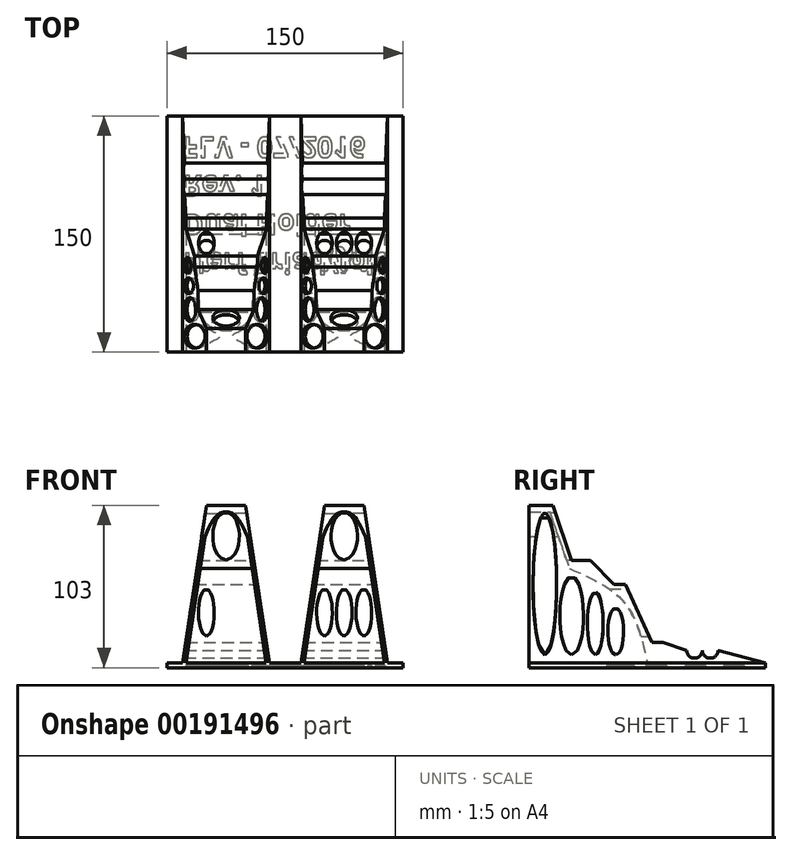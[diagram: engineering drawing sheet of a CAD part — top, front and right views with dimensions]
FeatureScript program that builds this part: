
annotation { "Feature Type Name" : "Feature", "Feature Type Description" : "" }
export const myFeature = defineFeature(function(context is Context, id is Id, definition is map)
    precondition{}
    {
        {
            var Q0;
            Q0=qCreatedBy(makeId("Top.planeOp"),FACE);
            var sketch = newSketch(context, id + "F0", { "sketchPlane" : qUnion([Q0])});
            skLineSegment(sketch, "E0.bottom", {"start": v(-75, 75) * mm, "end": v(75, 75) * mm});
            skLineSegment(sketch, "E0.top", {"start": v(-75, -75) * mm, "end": v(75, -75) * mm});
            skLineSegment(sketch, "E0.left", {"start": v(-75, 75) * mm, "end": v(-75, -75) * mm});
            skLineSegment(sketch, "E0.right", {"start": v(75, 75) * mm, "end": v(75, -75) * mm});
            skSolve(sketch);
        }
        {
            var Q0;
            Q0 = qSketchRegion(id + "F0", true);
            extrude(context, id + "F1", {"entities" : qUnion([Q0]), "depth" : 3 * mm});
        }
        {
            var Q0;
            Q0=makeQuery(id+"F1.opExtrude","SWEPT_FACE",FACE,{"disambiguationData":[OSD([sQuery(id+"F0.wireOp",EDGE,"E0.top")])]});
            var sketch = newSketch(context, id + "F2", { "sketchPlane" : qUnion([Q0])});
            skLineSegment(sketch, "E1.bottom", {"start": v(-75, 3) * mm, "end": v(75, 3) * mm});
            skLineSegment(sketch, "E1.top", {"start": v(-75, 103) * mm, "end": v(75, 103) * mm});
            skLineSegment(sketch, "E1.left", {"start": v(-75, 3) * mm, "end": v(-75, 103) * mm});
            skLineSegment(sketch, "E1.right", {"start": v(75, 3) * mm, "end": v(75, 103) * mm});
            skLineSegment(sketch, "E2", {"start": v(0, 3) * mm, "end": v(0, 103) * mm});
            skLineSegment(sketch, "E3", {"start": v(-50, 103) * mm, "end": v(-65, 3) * mm});
            skLineSegment(sketch, "E4", {"start": v(-25, 103) * mm, "end": v(-10, 3) * mm});
            skLineSegment(sketch, "E5", {"start": v(25, 103) * mm, "end": v(10, 3) * mm});
            skLineSegment(sketch, "E6", {"start": v(50, 103) * mm, "end": v(65, 3) * mm});
            skLineSegment(sketch, "E7", {"start": v(-62.98, 3) * mm, "end": v(-50.98, 83) * mm});
            skLineSegment(sketch, "E8", {"start": v(-12.02, 3) * mm, "end": v(-24.02, 83) * mm});
            skLineSegment(sketch, "E9", {"start": v(12.02, 3) * mm, "end": v(24.02, 83) * mm});
            skLineSegment(sketch, "E10", {"start": v(62.98, 3) * mm, "end": v(50.98, 83) * mm});
            skFitSpline(sketch, "E11", {"points": [v(-50.98, 83) * mm, v(-37.5, 99) * mm, v(-24.02, 83) * mm], "startDerivative": vector(32.87, 84) * mm, "endDerivative": vector(32.87, -84) * mm});
            skFitSpline(sketch, "E12", {"points": [v(24.02, 83) * mm, v(37.5, 99) * mm, v(50.98, 83) * mm], "startDerivative": vector(32.87, 84) * mm, "endDerivative": vector(32.87, -84) * mm});
            skSolve(sketch);
        }
        {
            var Q0;
            Q0=makeQuery(id+"F1.opExtrude","SWEPT_FACE",FACE,{"disambiguationData":[OSD([sQuery(id+"F0.wireOp",EDGE,"E0.right")])]});
            var sketch = newSketch(context, id + "F3", { "sketchPlane" : qUnion([Q0])});
            skLineSegment(sketch, "E13.bottom", {"start": v(-75, 3) * mm, "end": v(75, 3) * mm});
            skLineSegment(sketch, "E13.top", {"start": v(-75, 103) * mm, "end": v(75, 103) * mm});
            skLineSegment(sketch, "E13.left", {"start": v(-75, 3) * mm, "end": v(-75, 103) * mm});
            skLineSegment(sketch, "E13.right", {"start": v(75, 3) * mm, "end": v(75, 103) * mm});
            skLineSegment(sketch, "E14", {"start": v(-60, 103) * mm, "end": v(-48, 68) * mm});
            skLineSegment(sketch, "E15", {"start": v(-48, 68) * mm, "end": v(-36, 68) * mm});
            skLineSegment(sketch, "E16", {"start": v(-36, 68) * mm, "end": v(-21, 53) * mm});
            skLineSegment(sketch, "E17", {"start": v(-21, 53) * mm, "end": v(-14, 53) * mm});
            skLineSegment(sketch, "E18", {"start": v(-14, 53) * mm, "end": v(3, 16) * mm});
            skLineSegment(sketch, "E19", {"start": v(3, 16) * mm, "end": v(10, 16) * mm});
            skLineSegment(sketch, "E20", {"start": v(10, 16) * mm, "end": v(25, 11) * mm});
            skLineSegment(sketch, "E21", {"start": v(25, 11) * mm, "end": v(45, 11) * mm});
            skLineSegment(sketch, "E22", {"start": v(45, 11) * mm, "end": v(75, 3) * mm});
            skLineSegment(sketch, "E23", {"start": v(-63.17, 103) * mm, "end": v(-49.46, 63) * mm});
            skFitSpline(sketch, "E24", {"points": [v(-49.46, 63) * mm, v(-14.36, 41.18) * mm, v(0, 3) * mm], "startDerivative": vector(80.28, -35.19) * mm, "endDerivative": vector(18.56, -84.87) * mm});
            skSolve(sketch);
        }
        {
            var Q0;
            {var subQ0=sQuery(id+"F2.wireOp",EDGE,"E3");Q0=makeQuery(id+"F2.imprint","IMPRINT",FACE,{"disambiguationData":[TD([[makeQuery(id+"F2.imprint","IMPRINT",EDGE,{"derivedFrom":subQ0}),1.0]])]});}
            var Q1;
            {var subQ0=sQuery(id+"F2.wireOp",EDGE,"E5");Q1=makeQuery(id+"F2.imprint","IMPRINT",FACE,{"disambiguationData":[TD([[makeQuery(id+"F2.imprint","IMPRINT",EDGE,{"derivedFrom":subQ0}),1.0]])]});}
            var Q2;
            Q2=makeQuery(id+"F1.opExtrude","SWEPT_FACE",FACE,{"disambiguationData":[OSD([sQuery(id+"F0.wireOp",EDGE,"E0.bottom")])]});
            extrude(context, id + "F4", {"entities" : qUnion([Q0, Q1]), "operationType" : NewBodyOperationType.ADD, "endBound" : BoundingType.UP_TO_SURFACE, "oppositeDirection" : true, "endBoundEntityFace" : qUnion([Q2]), "depth" : 25 * mm});
        }
        {
            var Q0;
            {var subQ0=sQuery(id+"F3.wireOp",EDGE,"E14");Q0=makeQuery(id+"F3.imprint","IMPRINT",FACE,{"disambiguationData":[TD([[makeQuery(id+"F3.imprint","IMPRINT",EDGE,{"derivedFrom":subQ0}),-1.0]])]});}
            var Q1;
            Q1=makeQuery(id+"F1.opExtrude","SWEPT_FACE",FACE,{"disambiguationData":[OSD([sQuery(id+"F0.wireOp",EDGE,"E0.left")])]});
            extrude(context, id + "F5", {"entities" : qUnion([Q0]), "operationType" : NewBodyOperationType.ADD, "endBound" : BoundingType.UP_TO_SURFACE, "oppositeDirection" : true, "endBoundEntityFace" : qUnion([Q1]), "depth" : 25 * mm});
        }
        {
            var Q0;
            {var subQ0=sQuery(id+"F2.wireOp",EDGE,"E1.left");Q0=makeQuery(id+"F2.imprint","IMPRINT",FACE,{"disambiguationData":[TD([[makeQuery(id+"F2.imprint","IMPRINT",EDGE,{"derivedFrom":subQ0}),-1.0]])]});}
            var Q1;
            {var subQ0=sQuery(id+"F2.wireOp",EDGE,"E2");Q1=makeQuery(id+"F2.imprint","IMPRINT",FACE,{"disambiguationData":[TD([[makeQuery(id+"F2.imprint","IMPRINT",EDGE,{"derivedFrom":subQ0}),1.0]])]});}
            var Q2;
            {var subQ0=sQuery(id+"F2.wireOp",EDGE,"E2");Q2=makeQuery(id+"F2.imprint","IMPRINT",FACE,{"disambiguationData":[TD([[makeQuery(id+"F2.imprint","IMPRINT",EDGE,{"derivedFrom":subQ0}),-1.0]])]});}
            var Q3;
            {var subQ0=sQuery(id+"F2.wireOp",EDGE,"E1.right");Q3=makeQuery(id+"F2.imprint","IMPRINT",FACE,{"disambiguationData":[TD([[makeQuery(id+"F2.imprint","IMPRINT",EDGE,{"derivedFrom":subQ0}),1.0]])]});}
            var Q4;
            {var subQ0=sQuery(id+"F2.wireOp",EDGE,"E1.top");var subQ1=sQuery(id+"F2.wireOp",EDGE,"E1.bottom");var subQ2=sQuery(id+"F0.wireOp",EDGE,"E0.bottom");Q4=makeQuery(id+"F4.boolean.opBoolean","MERGE",FACE,{"derivedFrom":[makeQuery(id+"F1.opExtrude","SWEPT_FACE",FACE,{"disambiguationData":[OSD([subQ2])]}),makeQuery(id+"F4.opExtrude","CAP_FACE",FACE,{"disambiguationData":[OSD([subQ2]),ownerDisambiguation([makeQuery(id+"F4.opExtrude","SWEPT_BODY",BODY,{"disambiguationData":[OSD([subQ1,subQ0,sQuery(id+"F2.wireOp",EDGE,"E3"),sQuery(id+"F2.wireOp",EDGE,"E4"),sQuery(id+"F2.wireOp",EDGE,"E7"),sQuery(id+"F2.wireOp",EDGE,"E8"),sQuery(id+"F2.wireOp",EDGE,"ciHklE4U-pB17-gafY-pSRJ-bKM6XeZEa9pb")])]})])],"isStart":false}),makeQuery(id+"F4.opExtrude","CAP_FACE",FACE,{"disambiguationData":[OSD([subQ2]),ownerDisambiguation([makeQuery(id+"F4.opExtrude","SWEPT_BODY",BODY,{"disambiguationData":[OSD([subQ1,subQ0,sQuery(id+"F2.wireOp",EDGE,"E5"),sQuery(id+"F2.wireOp",EDGE,"E6"),sQuery(id+"F2.wireOp",EDGE,"E9"),sQuery(id+"F2.wireOp",EDGE,"E10"),sQuery(id+"F2.wireOp",EDGE,"xGXNXY8u-arDx-ufjF-TU0i-VHOFZnnzQfJi")])]})])],"isStart":false})]});}
            extrude(context, id + "F6", {"entities" : qUnion([Q0, Q1, Q2, Q3]), "operationType" : NewBodyOperationType.REMOVE, "endBound" : BoundingType.UP_TO_SURFACE, "oppositeDirection" : true, "endBoundEntityFace" : qUnion([Q4]), "depth" : 25 * mm});
        }
        {
            var Q0;
            {var subQ1=sQuery(id+"F3.wireOp",EDGE,"E13.right");Q0=makeQuery(id+"F3.imprint","IMPRINT",FACE,{"disambiguationData":[TD([[makeQuery(id+"F3.imprint","IMPRINT",EDGE,{"derivedFrom":subQ1}),1.0]])]});}
            var Q1;
            {var subQ0=sQuery(id+"F0.wireOp",EDGE,"E0.left");Q1=makeQuery(id+"F5.boolean.opBoolean","MERGE",FACE,{"derivedFrom":[makeQuery(id+"F1.opExtrude","SWEPT_FACE",FACE,{"disambiguationData":[OSD([subQ0])]}),makeQuery(id+"F5.opExtrude","CAP_FACE",FACE,{"disambiguationData":[OSD([subQ0])],"isStart":false})]});}
            extrude(context, id + "F7", {"entities" : qUnion([Q0]), "operationType" : NewBodyOperationType.REMOVE, "endBound" : BoundingType.UP_TO_SURFACE, "oppositeDirection" : true, "endBoundEntityFace" : qUnion([Q1]), "depth" : 25 * mm});
        }
        {
            var Q0;
            {var subQ0=sQuery(id+"F0.wireOp",EDGE,"E0.right");Q0=makeQuery(id+"F3.imprint","IMPRINT",FACE,{"disambiguationData":[TD([[makeQuery(id+"F3.imprint","IMPRINT",EDGE,{"derivedFrom":makeQuery(id+"F1.opExtrude","CAP_EDGE",EDGE,{"disambiguationData":[OSD([subQ0])],"isStart":true})}),-1.0]])]});}
            var sketch = newSketch(context, id + "F8", { "sketchPlane" : qUnion([Q0])});
            skEllipse(sketch, "E25", {"center": v(-65, 53) * mm, "majorRadius": 45 * mm, "minorRadius": 7.5 * mm, "majorAxis": v(0, -1)});
            skEllipse(sketch, "E26", {"center": v(-48, 33) * mm, "majorRadius": 25 * mm, "minorRadius": 7.5 * mm, "majorAxis": v(0, -1)});
            skEllipse(sketch, "E27", {"center": v(-33, 28) * mm, "majorRadius": 20 * mm, "minorRadius": 5 * mm, "majorAxis": v(0, -1)});
            skEllipse(sketch, "E28", {"center": v(-20, 23) * mm, "majorRadius": 15 * mm, "minorRadius": 5 * mm, "majorAxis": v(0, -1)});
            skSolve(sketch);
        }
        {
            var Q0;
            Q0=makeQuery(id+"F8.imprint","IMPRINT",FACE,{"disambiguationData":[TD([[makeQuery(id+"F8.imprint","IMPRINT",EDGE,{"derivedFrom":sQuery(id+"F8.wireOp",EDGE,"E26")}),1.0]])]});
            var Q1;
            Q1=makeQuery(id+"F8.imprint","IMPRINT",FACE,{"disambiguationData":[TD([[makeQuery(id+"F8.imprint","IMPRINT",EDGE,{"derivedFrom":sQuery(id+"F8.wireOp",EDGE,"E25")}),1.0]])]});
            var Q2;
            Q2=makeQuery(id+"F8.imprint","IMPRINT",FACE,{"disambiguationData":[TD([[makeQuery(id+"F8.imprint","IMPRINT",EDGE,{"derivedFrom":sQuery(id+"F8.wireOp",EDGE,"E27")}),1.0]])]});
            var Q3;
            Q3=makeQuery(id+"F8.imprint","IMPRINT",FACE,{"disambiguationData":[TD([[makeQuery(id+"F8.imprint","IMPRINT",EDGE,{"derivedFrom":sQuery(id+"F8.wireOp",EDGE,"E28")}),1.0]])]});
            var Q4;
            {var subQ0=sQuery(id+"F0.wireOp",EDGE,"E0.left");Q4=makeQuery(id+"F5.boolean.opBoolean","MERGE",FACE,{"derivedFrom":[makeQuery(id+"F1.opExtrude","SWEPT_FACE",FACE,{"disambiguationData":[OSD([subQ0])]}),makeQuery(id+"F5.opExtrude","CAP_FACE",FACE,{"disambiguationData":[OSD([subQ0])],"isStart":false})]});}
            extrude(context, id + "F9", {"entities" : qUnion([Q0, Q1, Q2, Q3]), "operationType" : NewBodyOperationType.REMOVE, "endBound" : BoundingType.UP_TO_SURFACE, "oppositeDirection" : true, "endBoundEntityFace" : qUnion([Q4]), "depth" : 25 * mm});
        }
        {
            var Q0;
            {var subQ0=sQuery(id+"F2.wireOp",EDGE,"E1.top");var subQ1=sQuery(id+"F2.wireOp",EDGE,"E1.bottom");var subQ2=sQuery(id+"F0.wireOp",EDGE,"E0.bottom");Q0=makeQuery(id+"F4.boolean.opBoolean","MERGE",FACE,{"derivedFrom":[makeQuery(id+"F1.opExtrude","SWEPT_FACE",FACE,{"disambiguationData":[OSD([subQ2])]}),makeQuery(id+"F4.opExtrude","CAP_FACE",FACE,{"disambiguationData":[OSD([subQ2]),ownerDisambiguation([makeQuery(id+"F4.opExtrude","SWEPT_BODY",BODY,{"disambiguationData":[OSD([subQ1,subQ0,sQuery(id+"F2.wireOp",EDGE,"E3"),sQuery(id+"F2.wireOp",EDGE,"E4"),sQuery(id+"F2.wireOp",EDGE,"E7"),sQuery(id+"F2.wireOp",EDGE,"E8"),sQuery(id+"F2.wireOp",EDGE,"E11")])]})])],"isStart":false}),makeQuery(id+"F4.opExtrude","CAP_FACE",FACE,{"disambiguationData":[OSD([subQ2]),ownerDisambiguation([makeQuery(id+"F4.opExtrude","SWEPT_BODY",BODY,{"disambiguationData":[OSD([subQ1,subQ0,sQuery(id+"F2.wireOp",EDGE,"E5"),sQuery(id+"F2.wireOp",EDGE,"E6"),sQuery(id+"F2.wireOp",EDGE,"E9"),sQuery(id+"F2.wireOp",EDGE,"E10"),sQuery(id+"F2.wireOp",EDGE,"E12")])]})])],"isStart":false})]});}
            var sketch = newSketch(context, id + "F10", { "sketchPlane" : qUnion([Q0])});
            skLineSegment(sketch, "E29.bottom", {"start": v(-75, 3) * mm, "end": v(75, 3) * mm});
            skLineSegment(sketch, "E29.top", {"start": v(-75, 103) * mm, "end": v(75, 103) * mm});
            skLineSegment(sketch, "E29.left", {"start": v(-75, 3) * mm, "end": v(-75, 103) * mm});
            skLineSegment(sketch, "E29.right", {"start": v(75, 3) * mm, "end": v(75, 103) * mm});
            skLineSegment(sketch, "E30", {"start": v(0, 103) * mm, "end": v(0, 3) * mm});
            skEllipse(sketch, "E31", {"center": v(-50, 35) * mm, "majorRadius": 15 * mm, "minorRadius": 5 * mm, "majorAxis": v(0, -1)});
            skEllipse(sketch, "E32", {"center": v(-37.5, 35) * mm, "majorRadius": 15 * mm, "minorRadius": 5 * mm, "majorAxis": v(0, -1)});
            skEllipse(sketch, "E33", {"center": v(-25, 35) * mm, "majorRadius": 15 * mm, "minorRadius": 5 * mm, "majorAxis": v(0, -1)});
            skEllipse(sketch, "E34.MirrorC", {"center": v(50, 35) * mm, "majorRadius": 15 * mm, "minorRadius": 5 * mm, "majorAxis": v(0, -1)});
            skEllipse(sketch, "E35.MirrorC", {"center": v(25, 35) * mm, "majorRadius": 15 * mm, "minorRadius": 5 * mm, "majorAxis": v(0, -1)});
            skEllipse(sketch, "E36.MirrorC", {"center": v(37.5, 35) * mm, "majorRadius": 15 * mm, "minorRadius": 5 * mm, "majorAxis": v(0, -1)});
            skEllipse(sketch, "E37.MirrorC", {"center": v(25, 35) * mm, "majorRadius": 15 * mm, "minorRadius": 5 * mm, "majorAxis": v(0, -1)});
            skEllipse(sketch, "E38.MirrorC", {"center": v(37.5, 35) * mm, "majorRadius": 15 * mm, "minorRadius": 5 * mm, "majorAxis": v(0, -1)});
            skEllipse(sketch, "E39", {"center": v(-37.5, 83.56) * mm, "majorRadius": 15 * mm, "minorRadius": 8.45 * mm, "majorAxis": v(0, -1)});
            skEllipse(sketch, "E40.MirrorC", {"center": v(37.5, 83.56) * mm, "majorRadius": 15 * mm, "minorRadius": 8.45 * mm, "majorAxis": v(0, -1)});
            skSolve(sketch);
        }
        {
            var Q0;
            Q0=makeQuery(id+"F10.imprint","IMPRINT",FACE,{"disambiguationData":[TD([[makeQuery(id+"F10.imprint","IMPRINT",EDGE,{"derivedFrom":sQuery(id+"F10.wireOp",EDGE,"E31")}),1.0]])]});
            var Q1;
            Q1=makeQuery(id+"F10.imprint","IMPRINT",FACE,{"disambiguationData":[TD([[makeQuery(id+"F10.imprint","IMPRINT",EDGE,{"derivedFrom":sQuery(id+"F10.wireOp",EDGE,"E32")}),1.0]])]});
            var Q2;
            Q2=makeQuery(id+"F10.imprint","IMPRINT",FACE,{"disambiguationData":[TD([[makeQuery(id+"F10.imprint","IMPRINT",EDGE,{"derivedFrom":sQuery(id+"F10.wireOp",EDGE,"E33")}),1.0]])]});
            var Q3;
            Q3=makeQuery(id+"F10.imprint","IMPRINT",FACE,{"disambiguationData":[TD([[makeQuery(id+"F10.imprint","IMPRINT",EDGE,{"derivedFrom":sQuery(id+"F10.wireOp",EDGE,"E37.MirrorC")}),1.0]])]});
            var Q4;
            Q4=makeQuery(id+"F10.imprint","IMPRINT",FACE,{"disambiguationData":[TD([[makeQuery(id+"F10.imprint","IMPRINT",EDGE,{"derivedFrom":sQuery(id+"F10.wireOp",EDGE,"E34.MirrorC")}),1.0]])]});
            var Q5;
            Q5=makeQuery(id+"F10.imprint","IMPRINT",FACE,{"disambiguationData":[TD([[makeQuery(id+"F10.imprint","IMPRINT",EDGE,{"derivedFrom":sQuery(id+"F10.wireOp",EDGE,"E38.MirrorC")}),1.0]])]});
            var Q6;
            Q6=makeQuery(id+"F10.imprint","IMPRINT",FACE,{"disambiguationData":[TD([[makeQuery(id+"F10.imprint","IMPRINT",EDGE,{"derivedFrom":sQuery(id+"F10.wireOp",EDGE,"E39")}),1.0]])]});
            var Q7;
            Q7=makeQuery(id+"F10.imprint","IMPRINT",FACE,{"disambiguationData":[TD([[makeQuery(id+"F10.imprint","IMPRINT",EDGE,{"derivedFrom":sQuery(id+"F10.wireOp",EDGE,"E40.MirrorC")}),1.0]])]});
            var Q8;
            {var subQ0=sQuery(id+"F2.wireOp",EDGE,"E1.top");var subQ1=sQuery(id+"F2.wireOp",EDGE,"E1.bottom");Q8=makeQuery(id+"F4.boolean.opBoolean","MERGE",FACE,{"derivedFrom":[makeQuery(id+"F1.opExtrude","SWEPT_FACE",FACE,{"disambiguationData":[OSD([sQuery(id+"F0.wireOp",EDGE,"E0.top")])]}),makeQuery(id+"F4.opExtrude","CAP_FACE",FACE,{"disambiguationData":[OSD([subQ1,subQ0,sQuery(id+"F2.wireOp",EDGE,"E3"),sQuery(id+"F2.wireOp",EDGE,"E4"),sQuery(id+"F2.wireOp",EDGE,"E7"),sQuery(id+"F2.wireOp",EDGE,"E8"),sQuery(id+"F2.wireOp",EDGE,"E11")])],"isStart":true}),makeQuery(id+"F4.opExtrude","CAP_FACE",FACE,{"disambiguationData":[OSD([subQ1,subQ0,sQuery(id+"F2.wireOp",EDGE,"E5"),sQuery(id+"F2.wireOp",EDGE,"E6"),sQuery(id+"F2.wireOp",EDGE,"E9"),sQuery(id+"F2.wireOp",EDGE,"E10"),sQuery(id+"F2.wireOp",EDGE,"E12")])],"isStart":true})]});}
            extrude(context, id + "F11", {"entities" : qUnion([Q0, Q1, Q2, Q3, Q4, Q5, Q6, Q7]), "operationType" : NewBodyOperationType.REMOVE, "endBound" : BoundingType.UP_TO_SURFACE, "oppositeDirection" : true, "endBoundEntityFace" : qUnion([Q8]), "depth" : 25 * mm});
        }
        {
            var Q0;
            {var subQ0=sQuery(id+"F0.wireOp",EDGE,"E0.right");Q0=makeQuery(id+"F3.imprint","IMPRINT",FACE,{"disambiguationData":[TD([[makeQuery(id+"F3.imprint","IMPRINT",EDGE,{"derivedFrom":makeQuery(id+"F1.opExtrude","CAP_EDGE",EDGE,{"disambiguationData":[OSD([subQ0])],"isStart":true})}),-1.0]])]});}
            cPlane(context, id + "F12", {"entities" : qUnion([Q0]), "cplaneType" : CPlaneType.OFFSET, "offset" : 37.5 * mm, "oppositeDirection" : true, "width" : 150 * mm, "height" : 150 * mm});
        }
        {
            var Q0;
            {var subQ0=sQuery(id+"F3.wireOp",EDGE,"E21");Q0=makeQuery(id+"F7.boolean.opBoolean","MERGE",FACE,{"derivedFrom":[makeQuery(id+"F5.boolean.opBoolean","SPLIT",FACE,{"disambiguationData":[TD([makeQuery(id+"F4.opExtrude","SWEPT_FACE",FACE,{"disambiguationData":[OSD([sQuery(id+"F2.wireOp",EDGE,"E7")])]})])],"derivedFrom":makeQuery(id+"F5.opExtrude","SWEPT_FACE",FACE,{"disambiguationData":[OSD([subQ0])]})}),makeQuery(id+"F7.opExtrude","SWEPT_FACE",FACE,{"disambiguationData":[OSD([subQ0])]})]});}
            var sketch = newSketch(context, id + "F13", { "sketchPlane" : qUnion([Q0])});
            skLineSegment(sketch, "E41.bottom", {"start": v(-64.8, 45) * mm, "end": v(-10.2, 45) * mm});
            skLineSegment(sketch, "E41.top", {"start": v(-64.8, 25) * mm, "end": v(-10.2, 25) * mm});
            skLineSegment(sketch, "E41.left", {"start": v(-64.8, 45) * mm, "end": v(-64.8, 25) * mm});
            skLineSegment(sketch, "E41.right", {"start": v(-10.2, 45) * mm, "end": v(-10.2, 25) * mm});
            skLineSegment(sketch, "E42", {"start": v(-64.8, 35) * mm, "end": v(-10.2, 35) * mm});
            skLineSegment(sketch, "E43", {"start": v(-64.8, 30) * mm, "end": v(-10.2, 30) * mm});
            skLineSegment(sketch, "E44", {"start": v(-10.2, 40) * mm, "end": v(-64.8, 40) * mm});
            skSolve(sketch);
        }
        {
            var Q0;
            {var subQ0=sQuery(id+"F13.wireOp",EDGE,"E42");var subQ1=sQuery(id+"F3.wireOp",EDGE,"E21");var subQ2=makeQuery(id+"F7.opExtrude","SWEPT_FACE",FACE,{"disambiguationData":[OSD([subQ1])]});var subQ3=sQuery(id+"F2.wireOp",EDGE,"E3");var subQ5=sQuery(id+"F0.wireOp",EDGE,"E0.bottom");var subQ6=makeQuery(id+"F1.opExtrude","SWEPT_FACE",FACE,{"disambiguationData":[OSD([subQ5])]});var subQ31=makeQuery(id+"F4.opExtrude","SWEPT_FACE",FACE,{"disambiguationData":[OSD([subQ3])]});var subQ34=sQuery(id+"F0.wireOp",EDGE,"E0.top");var subQ35=makeQuery(id+"F1.opExtrude","SWEPT_FACE",FACE,{"disambiguationData":[OSD([subQ34])]});var subQ39=makeQuery(id+"F7.boolean.opBoolean","INTERSECT",EDGE,{"derivedFrom":[makeQuery(id+"F6.boolean.opBoolean","MERGE",FACE,{"derivedFrom":[makeQuery(id+"F5.boolean.opBoolean","SPLIT",FACE,{"disambiguationData":[TD([subQ35])],"derivedFrom":subQ31}),makeQuery(id+"F5.boolean.opBoolean","SPLIT",FACE,{"disambiguationData":[TD([subQ6])],"derivedFrom":subQ31}),makeQuery(id+"F6.opExtrude","SWEPT_FACE",FACE,{"disambiguationData":[OSD([subQ3])]})]}),subQ2]});var subQ40=makeQuery(id+"F13.imprint","INTERSECT",VERTEX,{"derivedFrom":[subQ39,subQ0]});Q0=makeQuery(id+"F13.imprint","IMPRINT",FACE,{"disambiguationData":[TD([[makeQuery(id+"F13.imprint","IMPRINT",EDGE,{"disambiguationData":[TD([[subQ40,-1.0]])],"derivedFrom":subQ0}),1.0]])]});}
            var Q1;
            {var subQ0=sQuery(id+"F13.wireOp",EDGE,"E42");var subQ1=sQuery(id+"F13.wireOp",EDGE,"E41.right");var subQ2=makeQuery(id+"F13.imprint","INTERSECT",VERTEX,{"derivedFrom":[subQ1,subQ0]});Q1=makeQuery(id+"F13.imprint","IMPRINT",FACE,{"disambiguationData":[TD([[makeQuery(id+"F13.imprint","IMPRINT",EDGE,{"disambiguationData":[TD([[subQ2,1.0]])],"derivedFrom":subQ1}),-1.0]])]});}
            var Q2;
            {var subQ0=sQuery(id+"F13.wireOp",EDGE,"E42");var subQ1=sQuery(id+"F13.wireOp",EDGE,"E41.left");var subQ2=makeQuery(id+"F13.imprint","INTERSECT",VERTEX,{"derivedFrom":[subQ1,subQ0]});Q2=makeQuery(id+"F13.imprint","IMPRINT",FACE,{"disambiguationData":[TD([[makeQuery(id+"F13.imprint","IMPRINT",EDGE,{"disambiguationData":[TD([[subQ2,1.0]])],"derivedFrom":subQ1}),1.0]])]});}
            var Q3;
            Q3=sQuery(id+"F13.wireOp",EDGE,"E44");
            revolve(context, id + "F14", {"operationType" : NewBodyOperationType.REMOVE, "entities" : qUnion([Q0, Q1, Q2]), "axis" : qUnion([Q3]), "revolveType" : RevolveType.FULL, "oppositeDirection" : true});
        }
        {
            var Q0;
            {var subQ0=sQuery(id+"F13.wireOp",EDGE,"E42");var subQ1=sQuery(id+"F3.wireOp",EDGE,"E21");var subQ2=makeQuery(id+"F7.opExtrude","SWEPT_FACE",FACE,{"disambiguationData":[OSD([subQ1])]});var subQ3=sQuery(id+"F2.wireOp",EDGE,"E3");var subQ5=sQuery(id+"F0.wireOp",EDGE,"E0.bottom");var subQ6=makeQuery(id+"F1.opExtrude","SWEPT_FACE",FACE,{"disambiguationData":[OSD([subQ5])]});var subQ31=makeQuery(id+"F4.opExtrude","SWEPT_FACE",FACE,{"disambiguationData":[OSD([subQ3])]});var subQ34=sQuery(id+"F0.wireOp",EDGE,"E0.top");var subQ35=makeQuery(id+"F1.opExtrude","SWEPT_FACE",FACE,{"disambiguationData":[OSD([subQ34])]});var subQ39=makeQuery(id+"F7.boolean.opBoolean","INTERSECT",EDGE,{"derivedFrom":[makeQuery(id+"F6.boolean.opBoolean","MERGE",FACE,{"derivedFrom":[makeQuery(id+"F5.boolean.opBoolean","SPLIT",FACE,{"disambiguationData":[TD([subQ35])],"derivedFrom":subQ31}),makeQuery(id+"F5.boolean.opBoolean","SPLIT",FACE,{"disambiguationData":[TD([subQ6])],"derivedFrom":subQ31}),makeQuery(id+"F6.opExtrude","SWEPT_FACE",FACE,{"disambiguationData":[OSD([subQ3])]})]}),subQ2]});var subQ40=makeQuery(id+"F13.imprint","INTERSECT",VERTEX,{"derivedFrom":[subQ39,subQ0]});Q0=makeQuery(id+"F13.imprint","IMPRINT",FACE,{"disambiguationData":[TD([[makeQuery(id+"F13.imprint","IMPRINT",EDGE,{"disambiguationData":[TD([[subQ40,-1.0]])],"derivedFrom":subQ0}),-1.0]])]});}
            var Q1;
            {var subQ0=sQuery(id+"F13.wireOp",EDGE,"E42");var subQ1=sQuery(id+"F13.wireOp",EDGE,"E41.left");var subQ2=makeQuery(id+"F13.imprint","INTERSECT",VERTEX,{"derivedFrom":[subQ1,subQ0]});Q1=makeQuery(id+"F13.imprint","IMPRINT",FACE,{"disambiguationData":[TD([[makeQuery(id+"F13.imprint","IMPRINT",EDGE,{"disambiguationData":[TD([[subQ2,-1.0]])],"derivedFrom":subQ1}),1.0]])]});}
            var Q2;
            {var subQ0=sQuery(id+"F13.wireOp",EDGE,"E42");var subQ1=sQuery(id+"F13.wireOp",EDGE,"E41.right");var subQ2=makeQuery(id+"F13.imprint","INTERSECT",VERTEX,{"derivedFrom":[subQ1,subQ0]});Q2=makeQuery(id+"F13.imprint","IMPRINT",FACE,{"disambiguationData":[TD([[makeQuery(id+"F13.imprint","IMPRINT",EDGE,{"disambiguationData":[TD([[subQ2,-1.0]])],"derivedFrom":subQ1}),-1.0]])]});}
            var Q3;
            Q3=sQuery(id+"F13.wireOp",EDGE,"E43");
            revolve(context, id + "F15", {"operationType" : NewBodyOperationType.REMOVE, "entities" : qUnion([Q0, Q1, Q2]), "axis" : qUnion([Q3]), "revolveType" : RevolveType.FULL, "oppositeDirection" : true});
        }
        {
            var Q0;
            {var subQ0=sQuery(id+"F3.wireOp",EDGE,"E21");Q0=makeQuery(id+"F7.boolean.opBoolean","MERGE",FACE,{"derivedFrom":[makeQuery(id+"F5.boolean.opBoolean","SPLIT",FACE,{"disambiguationData":[TD([makeQuery(id+"F4.opExtrude","SWEPT_FACE",FACE,{"disambiguationData":[OSD([sQuery(id+"F2.wireOp",EDGE,"E9")])]})])],"derivedFrom":makeQuery(id+"F5.opExtrude","SWEPT_FACE",FACE,{"disambiguationData":[OSD([subQ0])]})}),makeQuery(id+"F7.opExtrude","SWEPT_FACE",FACE,{"disambiguationData":[OSD([subQ0])]})]});}
            var sketch = newSketch(context, id + "F16", { "sketchPlane" : qUnion([Q0])});
            skLineSegment(sketch, "E45.bottom", {"start": v(10.2, 45) * mm, "end": v(64.8, 45) * mm});
            skLineSegment(sketch, "E45.top", {"start": v(10.2, 25) * mm, "end": v(64.8, 25) * mm});
            skLineSegment(sketch, "E45.left", {"start": v(10.2, 45) * mm, "end": v(10.2, 25) * mm});
            skLineSegment(sketch, "E45.right", {"start": v(64.8, 45) * mm, "end": v(64.8, 25) * mm});
            skLineSegment(sketch, "E46", {"start": v(10.2, 35) * mm, "end": v(64.8, 35) * mm});
            skLineSegment(sketch, "E47", {"start": v(64.8, 30) * mm, "end": v(10.2, 30) * mm});
            skLineSegment(sketch, "E48", {"start": v(10.2, 40) * mm, "end": v(64.8, 40) * mm});
            skSolve(sketch);
        }
        {
            var Q0;
            {var subQ0=sQuery(id+"F16.wireOp",EDGE,"E46");var subQ1=sQuery(id+"F3.wireOp",EDGE,"E21");var subQ2=makeQuery(id+"F7.opExtrude","SWEPT_FACE",FACE,{"disambiguationData":[OSD([subQ1])]});var subQ3=sQuery(id+"F2.wireOp",EDGE,"E5");var subQ5=sQuery(id+"F0.wireOp",EDGE,"E0.bottom");var subQ6=makeQuery(id+"F1.opExtrude","SWEPT_FACE",FACE,{"disambiguationData":[OSD([subQ5])]});var subQ31=makeQuery(id+"F4.opExtrude","SWEPT_FACE",FACE,{"disambiguationData":[OSD([subQ3])]});var subQ34=sQuery(id+"F0.wireOp",EDGE,"E0.top");var subQ35=makeQuery(id+"F1.opExtrude","SWEPT_FACE",FACE,{"disambiguationData":[OSD([subQ34])]});var subQ39=makeQuery(id+"F7.boolean.opBoolean","INTERSECT",EDGE,{"derivedFrom":[makeQuery(id+"F6.boolean.opBoolean","MERGE",FACE,{"derivedFrom":[makeQuery(id+"F5.boolean.opBoolean","SPLIT",FACE,{"disambiguationData":[TD([subQ35])],"derivedFrom":subQ31}),makeQuery(id+"F5.boolean.opBoolean","SPLIT",FACE,{"disambiguationData":[TD([subQ6])],"derivedFrom":subQ31}),makeQuery(id+"F6.opExtrude","SWEPT_FACE",FACE,{"disambiguationData":[OSD([subQ3])]})]}),subQ2]});var subQ40=makeQuery(id+"F16.imprint","INTERSECT",VERTEX,{"derivedFrom":[subQ39,subQ0]});Q0=makeQuery(id+"F16.imprint","IMPRINT",FACE,{"disambiguationData":[TD([[makeQuery(id+"F16.imprint","IMPRINT",EDGE,{"disambiguationData":[TD([[subQ40,-1.0]])],"derivedFrom":subQ0}),1.0]])]});}
            var Q1;
            {var subQ0=sQuery(id+"F16.wireOp",EDGE,"E46");var subQ1=sQuery(id+"F16.wireOp",EDGE,"E45.left");var subQ2=makeQuery(id+"F16.imprint","INTERSECT",VERTEX,{"derivedFrom":[subQ1,subQ0]});Q1=makeQuery(id+"F16.imprint","IMPRINT",FACE,{"disambiguationData":[TD([[makeQuery(id+"F16.imprint","IMPRINT",EDGE,{"disambiguationData":[TD([[subQ2,1.0]])],"derivedFrom":subQ1}),1.0]])]});}
            var Q2;
            {var subQ0=sQuery(id+"F16.wireOp",EDGE,"E46");var subQ1=sQuery(id+"F16.wireOp",EDGE,"E45.right");var subQ2=makeQuery(id+"F16.imprint","INTERSECT",VERTEX,{"derivedFrom":[subQ1,subQ0]});Q2=makeQuery(id+"F16.imprint","IMPRINT",FACE,{"disambiguationData":[TD([[makeQuery(id+"F16.imprint","IMPRINT",EDGE,{"disambiguationData":[TD([[subQ2,1.0]])],"derivedFrom":subQ1}),-1.0]])]});}
            var Q3;
            Q3=sQuery(id+"F16.wireOp",EDGE,"E48");
            revolve(context, id + "F17", {"operationType" : NewBodyOperationType.REMOVE, "entities" : qUnion([Q0, Q1, Q2]), "axis" : qUnion([Q3]), "revolveType" : RevolveType.FULL});
        }
        {
            var Q0;
            {var subQ0=sQuery(id+"F16.wireOp",EDGE,"E46");var subQ1=sQuery(id+"F3.wireOp",EDGE,"E21");var subQ2=makeQuery(id+"F7.opExtrude","SWEPT_FACE",FACE,{"disambiguationData":[OSD([subQ1])]});var subQ3=sQuery(id+"F2.wireOp",EDGE,"E5");var subQ5=sQuery(id+"F0.wireOp",EDGE,"E0.bottom");var subQ6=makeQuery(id+"F1.opExtrude","SWEPT_FACE",FACE,{"disambiguationData":[OSD([subQ5])]});var subQ31=makeQuery(id+"F4.opExtrude","SWEPT_FACE",FACE,{"disambiguationData":[OSD([subQ3])]});var subQ34=sQuery(id+"F0.wireOp",EDGE,"E0.top");var subQ35=makeQuery(id+"F1.opExtrude","SWEPT_FACE",FACE,{"disambiguationData":[OSD([subQ34])]});var subQ39=makeQuery(id+"F7.boolean.opBoolean","INTERSECT",EDGE,{"derivedFrom":[makeQuery(id+"F6.boolean.opBoolean","MERGE",FACE,{"derivedFrom":[makeQuery(id+"F5.boolean.opBoolean","SPLIT",FACE,{"disambiguationData":[TD([subQ35])],"derivedFrom":subQ31}),makeQuery(id+"F5.boolean.opBoolean","SPLIT",FACE,{"disambiguationData":[TD([subQ6])],"derivedFrom":subQ31}),makeQuery(id+"F6.opExtrude","SWEPT_FACE",FACE,{"disambiguationData":[OSD([subQ3])]})]}),subQ2]});var subQ40=makeQuery(id+"F16.imprint","INTERSECT",VERTEX,{"derivedFrom":[subQ39,subQ0]});Q0=makeQuery(id+"F16.imprint","IMPRINT",FACE,{"disambiguationData":[TD([[makeQuery(id+"F16.imprint","IMPRINT",EDGE,{"disambiguationData":[TD([[subQ40,-1.0]])],"derivedFrom":subQ0}),-1.0]])]});}
            var Q1;
            {var subQ0=sQuery(id+"F16.wireOp",EDGE,"E46");var subQ1=sQuery(id+"F16.wireOp",EDGE,"E45.left");var subQ2=makeQuery(id+"F16.imprint","INTERSECT",VERTEX,{"derivedFrom":[subQ1,subQ0]});Q1=makeQuery(id+"F16.imprint","IMPRINT",FACE,{"disambiguationData":[TD([[makeQuery(id+"F16.imprint","IMPRINT",EDGE,{"disambiguationData":[TD([[subQ2,-1.0]])],"derivedFrom":subQ1}),1.0]])]});}
            var Q2;
            {var subQ0=sQuery(id+"F16.wireOp",EDGE,"E46");var subQ1=sQuery(id+"F16.wireOp",EDGE,"E45.right");var subQ2=makeQuery(id+"F16.imprint","INTERSECT",VERTEX,{"derivedFrom":[subQ1,subQ0]});Q2=makeQuery(id+"F16.imprint","IMPRINT",FACE,{"disambiguationData":[TD([[makeQuery(id+"F16.imprint","IMPRINT",EDGE,{"disambiguationData":[TD([[subQ2,-1.0]])],"derivedFrom":subQ1}),-1.0]])]});}
            var Q3;
            Q3=sQuery(id+"F16.wireOp",EDGE,"E47");
            revolve(context, id + "F18", {"operationType" : NewBodyOperationType.REMOVE, "entities" : qUnion([Q0, Q1, Q2]), "axis" : qUnion([Q3]), "revolveType" : RevolveType.FULL});
        }
        {
            var Q0;
            Q0=makeQuery(id+"F1.opExtrude","CAP_FACE",FACE,{"disambiguationData":[OSD([sQuery(id+"F0.wireOp",EDGE,"E0.bottom"),sQuery(id+"F0.wireOp",EDGE,"E0.top"),sQuery(id+"F0.wireOp",EDGE,"E0.left"),sQuery(id+"F0.wireOp",EDGE,"E0.right")])],"isStart":true});
            var sketch = newSketch(context, id + "F19", { "sketchPlane" : qUnion([Q0])});
            skText(sketch, "E49", { "text": "Nerf Triad/Jolt\nDual Holder\nRev. 1\nFLV - 07/2016", "fontName": "OpenSans-Bold.ttf"});
            const initialGuessF19  = {"E49": [-0.065, 0.01203, 1, 0, 0.01297]};
            skSetInitialGuess(sketch, initialGuessF19);
            skSolve(sketch);
        }
        {
            var Q0;
            Q0 = qSketchRegion(id + "F19", true);
            extrude(context, id + "F20", {"entities" : qUnion([Q0]), "operationType" : NewBodyOperationType.REMOVE, "oppositeDirection" : true, "depth" : 1 * mm});
        }
    });
